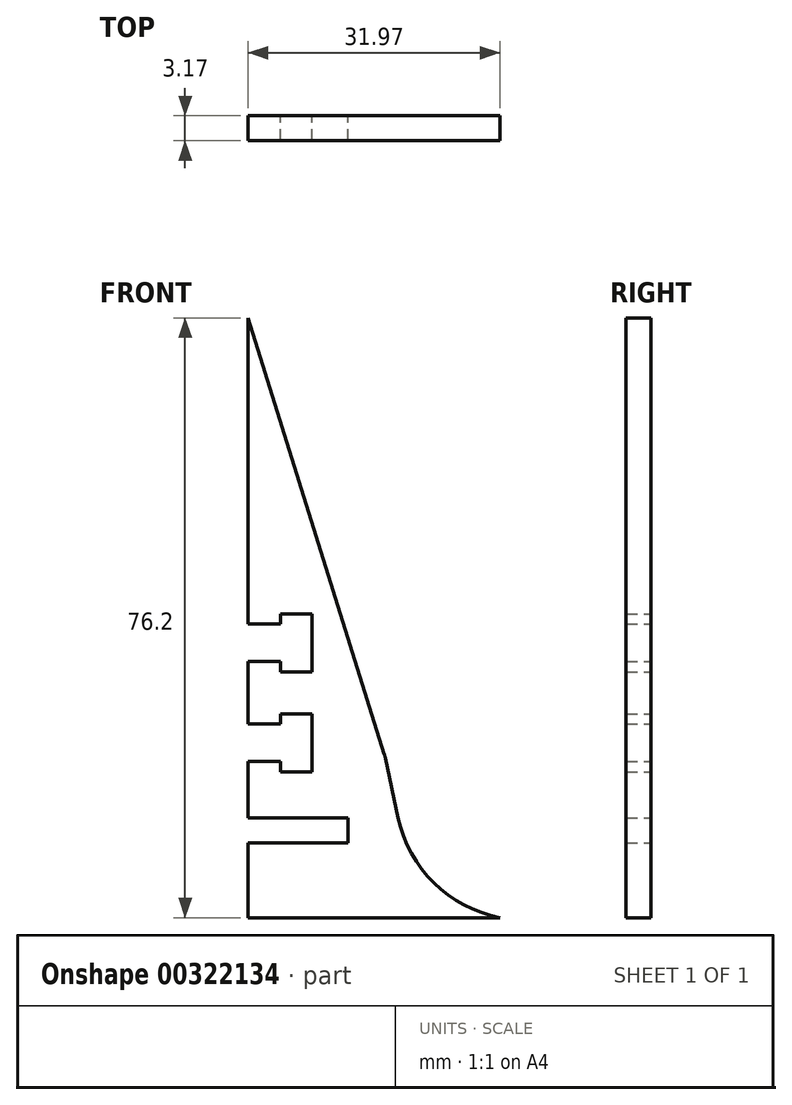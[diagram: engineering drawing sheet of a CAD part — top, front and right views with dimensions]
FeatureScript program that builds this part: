
annotation { "Feature Type Name" : "Feature", "Feature Type Description" : "" }
export const myFeature = defineFeature(function(context is Context, id is Id, definition is map)
    precondition{}
    {
        {
            var Q0;
            Q0=qCreatedBy(makeId("Front.planeOp"),FACE);
            var sketch = newSketch(context, id + "F0", { "sketchPlane" : qUnion([Q0])});
            skLineSegment(sketch, "E0.bottom", {"start": v(-12.7, 50.8) * mm, "end": v(19.05, 50.8) * mm, "construction": true});
            skLineSegment(sketch, "E0.top", {"start": v(-12.7, -76.2) * mm, "end": v(19.27, -76.2) * mm, "construction": true});
            skLineSegment(sketch, "E0.right", {"start": v(19.05, 50.8) * mm, "end": v(19.27, -76.2) * mm, "construction": true});
            skLineSegment(sketch, "E1", {"start": v(-12.7, 50.8) * mm, "end": v(-12.7, -76.2) * mm, "construction": true});
            skLineSegment(sketch, "E2", {"start": v(-12.7, -63.5) * mm, "end": v(0, -63.5) * mm, "construction": true});
            skLineSegment(sketch, "E3", {"start": v(0, -63.5) * mm, "end": v(0, -66.67) * mm, "construction": true});
            skLineSegment(sketch, "E4", {"start": v(-12.7, -66.67) * mm, "end": v(0, -66.67) * mm, "construction": true});
            skPoint(sketch, "E5", {"position": v(6.35, -63.5) * mm});
            skPoint(sketch, "E6", {"position": v(25.62, -76.2) * mm});
            skArc(sketch, "E7", {"start": v(6.35, -63.5) * mm, "mid": v(10.9, -71.79) * mm, "end": v(19.27, -76.2) * mm});
            skLineSegment(sketch, "E8", {"start": v(6.35, -63.5) * mm, "end": v(4.73, -55.94) * mm});
            skLineSegment(sketch, "E9", {"start": v(4.58, -55.38) * mm, "end": v(-12.7, 0) * mm});
            skPoint(sketch, "E10.visualSharp", {"position": v(4.67, -55.65) * mm});
            skArc(sketch, "E10.filletArc", {"start": v(4.73, -55.94) * mm, "mid": v(4.66, -55.65) * mm, "end": v(4.58, -55.38) * mm});
            skLineSegment(sketch, "E11", {"start": v(-12.7, 0) * mm, "end": v(-12.7, -76.2) * mm});
            skLineSegment(sketch, "E12", {"start": v(19.27, -76.2) * mm, "end": v(-12.7, -76.2) * mm});
            skLineSegment(sketch, "E13", {"start": v(19.27, -76.2) * mm, "end": v(19.27, -76.17) * mm});
            skLineSegment(sketch, "E14", {"start": v(-12.7, -63.5) * mm, "end": v(0, -63.5) * mm});
            skLineSegment(sketch, "E15", {"start": v(-12.7, -66.67) * mm, "end": v(0, -66.67) * mm});
            skLineSegment(sketch, "E16", {"start": v(0, -63.5) * mm, "end": v(0, -66.67) * mm});
            skLineSegment(sketch, "E17", {"start": v(-12.7, -56.36) * mm, "end": v(-8.59, -56.36) * mm});
            skLineSegment(sketch, "E18", {"start": v(-8.59, -51.6) * mm, "end": v(-12.7, -51.6) * mm});
            skLineSegment(sketch, "E19", {"start": v(-8.59, -51.6) * mm, "end": v(-8.59, -50.28) * mm});
            skLineSegment(sketch, "E20", {"start": v(-8.59, -50.28) * mm, "end": v(-4.62, -50.28) * mm});
            skLineSegment(sketch, "E21", {"start": v(-4.62, -50.28) * mm, "end": v(-4.62, -57.67) * mm});
            skLineSegment(sketch, "E22", {"start": v(-4.62, -57.67) * mm, "end": v(-8.59, -57.67) * mm});
            skLineSegment(sketch, "E23", {"start": v(-8.59, -57.67) * mm, "end": v(-8.59, -56.36) * mm});
            skLineSegment(sketch, "E24.0.1.0", {"start": v(-8.59, -38.9) * mm, "end": v(-12.7, -38.9) * mm});
            skLineSegment(sketch, "E24.0.1.1", {"start": v(-8.59, -38.9) * mm, "end": v(-8.59, -37.58) * mm});
            skLineSegment(sketch, "E24.0.1.2", {"start": v(-8.59, -37.58) * mm, "end": v(-4.62, -37.58) * mm});
            skLineSegment(sketch, "E24.0.1.3", {"start": v(-4.62, -37.58) * mm, "end": v(-4.62, -44.97) * mm});
            skLineSegment(sketch, "E24.0.1.4", {"start": v(-8.59, -44.97) * mm, "end": v(-8.59, -43.66) * mm});
            skLineSegment(sketch, "E24.0.1.5", {"start": v(-4.62, -44.97) * mm, "end": v(-8.59, -44.97) * mm});
            skLineSegment(sketch, "E24.0.1.6", {"start": v(-12.7, -43.66) * mm, "end": v(-8.59, -43.66) * mm});
            skLineSegment(sketch, "E24.direction1", {"start": v(-12.7, -56.36) * mm, "end": v(12.7, -56.36) * mm, "construction": true});
            skLineSegment(sketch, "E24.direction2", {"start": v(-12.7, -56.36) * mm, "end": v(-12.7, -43.66) * mm, "construction": true});
            skPoint(sketch, "E25", {"position": v(-12.7, -53.98) * mm});
            skPoint(sketch, "E25.positionSnap0", {"position": v(-4.62, -53.98) * mm});
            skPoint(sketch, "E26", {"position": v(-12.7, -41.27) * mm});
            skPoint(sketch, "E26.positionSnap0", {"position": v(-4.62, -41.27) * mm});
            skSolve(sketch);
        }
        {
            var Q0;
            {var subQ1=sQuery(id+"F0.wireOp",EDGE,"E8");Q0=makeQuery(id+"F0.imprint","IMPRINT",FACE,{"disambiguationData":[TD([[makeQuery(id+"F0.imprint","IMPRINT",EDGE,{"derivedFrom":subQ1}),1.0]])]});}
            extrude(context, id + "F1", {"entities" : qUnion([Q0]), "depth" : 3.17 * mm});
        }
    });
